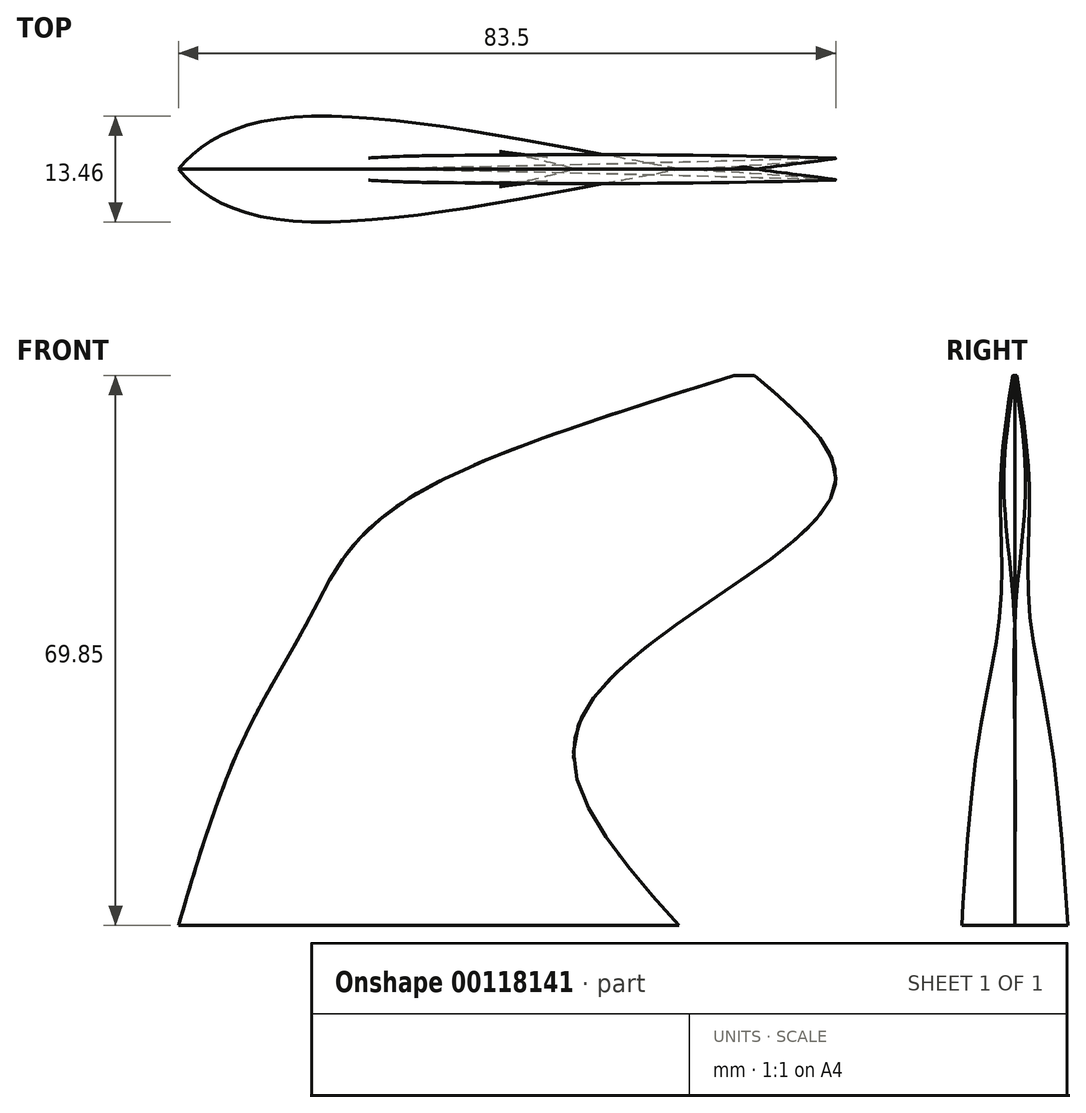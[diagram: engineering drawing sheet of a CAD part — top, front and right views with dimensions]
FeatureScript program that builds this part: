
annotation { "Feature Type Name" : "Feature", "Feature Type Description" : "" }
export const myFeature = defineFeature(function(context is Context, id is Id, definition is map)
    precondition{}
    {
        {
            var Q0;
            Q0=qCreatedBy(makeId("Top.planeOp"),FACE);
            var sketch = newSketch(context, id + "F0", { "sketchPlane" : qUnion([Q0])});
            skFitSpline(sketch, "E0", {"points": [v(0, 0) * mm, v(11.37, -6.2) * mm, v(63.59, 0) * mm], "startDerivative": vector(19.21, -24.21) * mm, "endDerivative": vector(97.38, 18.44) * mm});
            skLineSegment(sketch, "E1", {"start": v(0, 0) * mm, "end": v(63.59, 0) * mm});
            skSolve(sketch);
        }
        {
            var Q0;
            Q0=makeQuery(id+"F0.imprint","IMPRINT",FACE,{"disambiguationData":[TD([[makeQuery(id+"F0.imprint","IMPRINT",EDGE,{"derivedFrom":sQuery(id+"F0.wireOp",EDGE,"E0")}),1.0]])]});
            cPlane(context, id + "F1", {"entities" : qUnion([Q0]), "cplaneType" : CPlaneType.OFFSET, "offset" : 25.4 * mm, "width" : 152.4 * mm, "height" : 152.4 * mm});
        }
        {
            var Q0;
            Q0=qCreatedBy(id+"F1.planeOp",FACE);
            var sketch = newSketch(context, id + "F2", { "sketchPlane" : qUnion([Q0])});
            skFitSpline(sketch, "E2", {"points": [v(9.09, 0) * mm, v(15.35, -3.83) * mm, v(50.77, 0) * mm], "startDerivative": vector(18.1, -19.7) * mm, "endDerivative": vector(60.92, 16.07) * mm});
            skLineSegment(sketch, "E3", {"start": v(9.09, 0) * mm, "end": v(50.77, 0) * mm});
            skSolve(sketch);
        }
        {
            var Q0;
            Q0=makeQuery(id+"F2.imprint","IMPRINT",FACE,{"disambiguationData":[TD([[makeQuery(id+"F2.imprint","IMPRINT",EDGE,{"derivedFrom":sQuery(id+"F2.wireOp",EDGE,"E2")}),1.0]])]});
            cPlane(context, id + "F3", {"entities" : qUnion([Q0]), "cplaneType" : CPlaneType.OFFSET, "offset" : 12.7 * mm, "width" : 152.4 * mm, "height" : 152.4 * mm});
        }
        {
            var Q0;
            Q0=qCreatedBy(id+"F3.planeOp",FACE);
            var sketch = newSketch(context, id + "F4", { "sketchPlane" : qUnion([Q0])});
            skFitSpline(sketch, "E4", {"points": [v(16.15, 0) * mm, v(20.99, -1.68) * mm, v(63.06, 0) * mm], "startDerivative": vector(12.46, -12.74) * mm, "endDerivative": vector(72.03, 9.29) * mm});
            skLineSegment(sketch, "E5", {"start": v(16.15, 0) * mm, "end": v(63.06, 0) * mm});
            skSolve(sketch);
        }
        {
            var Q0;
            Q0=qCreatedBy(id+"F3.planeOp",FACE);
            cPlane(context, id + "F5", {"entities" : qUnion([Q0]), "cplaneType" : CPlaneType.OFFSET, "offset" : 19.05 * mm, "width" : 152.4 * mm, "height" : 152.4 * mm});
        }
        {
            var Q0;
            Q0=qCreatedBy(id+"F5.planeOp",FACE);
            var sketch = newSketch(context, id + "F6", { "sketchPlane" : qUnion([Q0])});
            skFitSpline(sketch, "E6", {"points": [v(34.61, 0) * mm, v(38.82, -1.67) * mm, v(83.5, -1.37) * mm], "startDerivative": vector(10.27, -20.53) * mm, "endDerivative": vector(82.24, 2.53) * mm});
            skLineSegment(sketch, "E7", {"start": v(83.5, -1.37) * mm, "end": v(34.61, 0) * mm});
            skSolve(sketch);
        }
        {
            var Q0;
            Q0=makeQuery(id+"F6.imprint","IMPRINT",FACE,{"disambiguationData":[TD([[makeQuery(id+"F6.imprint","IMPRINT",EDGE,{"derivedFrom":sQuery(id+"F6.wireOp",EDGE,"E6")}),1.0]])]});
            cPlane(context, id + "F7", {"entities" : qUnion([Q0]), "cplaneType" : CPlaneType.OFFSET, "offset" : 12.7 * mm, "width" : 152.4 * mm, "height" : 152.4 * mm});
        }
        {
            var Q0;
            Q0=qCreatedBy(id+"F7.planeOp",FACE);
            var sketch = newSketch(context, id + "F8", { "sketchPlane" : qUnion([Q0])});
            skFitSpline(sketch, "E8", {"points": [v(65.14, 0) * mm, v(70.54, 0) * mm, v(73.17, 0) * mm], "startDerivative": vector(10.55, 0) * mm, "endDerivative": vector(11.49, 3.53) * mm});
            skLineSegment(sketch, "E9", {"start": v(65.14, 0) * mm, "end": v(73.17, 0) * mm});
            skSolve(sketch);
        }
        {
            var Q0;
            Q0=makeQuery(id+"F0.imprint","IMPRINT",FACE,{"disambiguationData":[TD([[makeQuery(id+"F0.imprint","IMPRINT",EDGE,{"derivedFrom":sQuery(id+"F0.wireOp",EDGE,"E0")}),1.0]])]});
            var Q1;
            Q1=makeQuery(id+"F2.imprint","IMPRINT",FACE,{"disambiguationData":[TD([[makeQuery(id+"F2.imprint","IMPRINT",EDGE,{"derivedFrom":sQuery(id+"F2.wireOp",EDGE,"E2")}),1.0]])]});
            var Q2;
            Q2=makeQuery(id+"F4.imprint","IMPRINT",FACE,{"disambiguationData":[TD([[makeQuery(id+"F4.imprint","IMPRINT",EDGE,{"derivedFrom":sQuery(id+"F4.wireOp",EDGE,"E4")}),1.0]])]});
            var Q3;
            Q3=makeQuery(id+"F6.imprint","IMPRINT",FACE,{"disambiguationData":[TD([[makeQuery(id+"F6.imprint","IMPRINT",EDGE,{"derivedFrom":sQuery(id+"F6.wireOp",EDGE,"E6")}),1.0]])]});
            var Q4;
            Q4=makeQuery(id+"F8.imprint","IMPRINT",FACE,{"disambiguationData":[TD([[makeQuery(id+"F8.imprint","IMPRINT",EDGE,{"derivedFrom":sQuery(id+"F8.wireOp",EDGE,"E8")}),1.0]])]});
            loft(context, id + "F9", {"sheetProfilesArray" : [{ "sheetProfileEntities" : qUnion([Q0]) }, { "sheetProfileEntities" : qUnion([Q1]) }, { "sheetProfileEntities" : qUnion([Q2]) }, { "sheetProfileEntities" : qUnion([Q3]) }, { "sheetProfileEntities" : qUnion([Q4]) }]});
        }
        {
            var Q0;
            {var subQ0=sQuery(id+"F8.wireOp",EDGE,"E9");var subQ1=sQuery(id+"F8.wireOp",EDGE,"E8");var subQ2=makeQuery(id+"F8.imprint","INTERSECT",VERTEX,{"disambiguationData":[OD(1.0)],"derivedFrom":[subQ1,subQ0]});Q0=makeQuery(id+"F9.opLoft","SWEPT_BODY",BODY,{"disambiguationData":[OSD([makeQuery(id+"F0.imprint","IMPRINT",FACE,{"disambiguationData":[TD([[makeQuery(id+"F0.imprint","IMPRINT",EDGE,{"derivedFrom":sQuery(id+"F0.wireOp",EDGE,"E0")}),1.0]])]}),sQuery(id+"F2.wireOp",EDGE,"E3"),sQuery(id+"F4.wireOp",EDGE,"E5"),sQuery(id+"F6.wireOp",EDGE,"E7"),makeQuery(id+"F8.imprint","IMPRINT",FACE,{"disambiguationData":[TD([[makeQuery(id+"F8.imprint","IMPRINT",EDGE,{"disambiguationData":[TD([[subQ2,1.0]])],"derivedFrom":subQ1}),1.0]])]})])]});}
            var Q1;
            Q1=qCreatedBy(makeId("Front.planeOp"),FACE);
            mirror(context, id + "F10", {"entities" : qUnion([Q0]), "mirrorPlane" : qUnion([Q1])});
        }
    });
